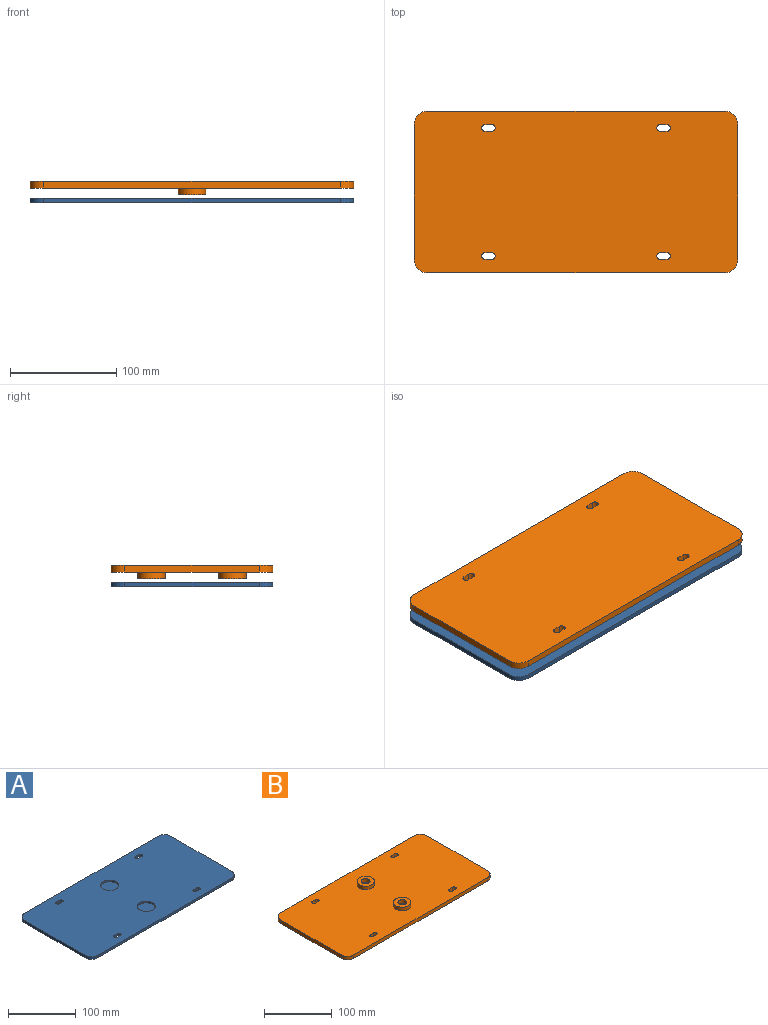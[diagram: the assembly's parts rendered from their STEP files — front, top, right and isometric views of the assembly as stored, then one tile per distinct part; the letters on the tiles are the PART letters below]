
ASSEMBLY  parts=2 mates=1
PART A: 30 faces, bbox 304.8x152.4x4.4 mm
  f0: plane 304.8x152.4mm, normal (0,0,1), area 44907.8mm2, adj f1,f2,f3,f4,f5,f6,f7,f8
  f1: plane 127x4.35mm, normal (1,0,0), area 552.5mm2, adj f0,f25,f28,f29
  f2: plane 279.4x4.35mm, normal (0,1,0), area 1215.4mm2, adj f0,f25,f26,f29
  f3: plane 127x4.35mm, normal (-1,0,0), area 552.5mm2, adj f0,f26,f27,f29
  f4: plane 279.4x4.35mm, normal (0,-1,0), area 1215.4mm2, adj f0,f27,f28,f29
  f5: plane 6.35x4.35mm, normal (0,-1,0), area 27.6mm2, adj f0,f6,f8,f29
  f6: cylinder r=3.17mm len=6.35mm, axis (0,0,1), area 43.4mm2, adj f0,f5,f7,f29
  f7: plane 6.35x4.35mm, normal (0,1,0), area 27.6mm2, adj f0,f6,f8,f29
  f8: cylinder r=3.17mm len=6.35mm, axis (0,0,1), area 43.4mm2, adj f0,f5,f7,f29
  f9: cylinder r=3.17mm len=6.35mm, axis (0,0,1), area 43.4mm2, adj f0,f10,f12,f29
  f10: plane 6.35x4.35mm, normal (0,-1,0), area 27.6mm2, adj f0,f9,f11,f29
  f11: cylinder r=3.17mm len=6.35mm, axis (0,0,1), area 43.4mm2, adj f0,f10,f12,f29
  f12: plane 6.35x4.35mm, normal (0,1,0), area 27.6mm2, adj f0,f9,f11,f29
  f13: cylinder r=3.17mm len=6.35mm, axis (0,0,1), area 43.4mm2, adj f0,f14,f16,f29
  f14: plane 6.35x4.35mm, normal (0,-1,0), area 27.6mm2, adj f0,f13,f15,f29
  f15: cylinder r=3.17mm len=6.35mm, axis (0,0,1), area 43.4mm2, adj f0,f14,f16,f29
  f16: plane 6.35x4.35mm, normal (0,1,0), area 27.6mm2, adj f0,f13,f15,f29
  f17: cylinder r=3.17mm len=6.35mm, axis (0,0,1), area 43.4mm2, adj f0,f18,f20,f29
  f18: plane 6.35x4.35mm, normal (0,-1,0), area 27.6mm2, adj f0,f17,f19,f29
  f19: cylinder r=3.17mm len=6.35mm, axis (0,0,1), area 43.4mm2, adj f0,f18,f20,f29
  f20: plane 6.35x4.35mm, normal (0,1,0), area 27.6mm2, adj f0,f17,f19,f29
  f21: cylinder r=13.33mm len=26.67mm, axis (0,0,1), area 266mm2, adj f0,f22
  f22: plane 26.67x26.67mm, normal (0,0,1), area 558.6mm2, adj f21
  f23: cylinder r=13.33mm len=26.67mm, axis (0,0,1), area 266mm2, adj f0,f24
  f24: plane 26.67x26.67mm, normal (0,0,1), area 558.6mm2, adj f23
  f25: cylinder r=12.7mm len=12.7mm, axis (0,0,1), area 86.8mm2, adj f0,f1,f2,f29
  f26: cylinder r=12.7mm len=12.7mm, axis (0,0,-1), area 86.8mm2, adj f0,f2,f3,f29
  f27: cylinder r=12.7mm len=12.7mm, axis (0,0,1), area 86.8mm2, adj f0,f3,f4,f29
  f28: cylinder r=12.7mm len=12.7mm, axis (0,0,-1), area 86.8mm2, adj f0,f1,f4,f29
  f29: plane 304.8x152.4mm, normal (0,0,-1), area 46025.1mm2, adj f1,f2,f3,f4,f5,f6,f7,f8
PART B: 34 faces, bbox 304.8x152.4x12.7 mm
  f0: plane 304.8x152.4mm, normal (0,0,1), area 44991.3mm2, adj f2,f3,f4,f5,f6,f7,f8,f9
  f1: plane 304.8x152.4mm, normal (0,0,-1), area 46025.1mm2, adj f2,f3,f4,f5,f6,f7,f8,f9
  f2: plane 279.4x6.35mm, normal (0,-1,0), area 1774.2mm2, adj f0,f1,f30,f33
  f3: plane 127x6.35mm, normal (1,0,0), area 806.5mm2, adj f0,f1,f30,f31
  f4: plane 279.4x6.35mm, normal (0,1,0), area 1774.2mm2, adj f0,f1,f31,f32
  f5: plane 127x6.35mm, normal (-1,0,0), area 806.5mm2, adj f0,f1,f32,f33
  f6: plane 6.35x6.35mm, normal (0,-1,0), area 40.3mm2, adj f0,f1,f7,f9
  f7: cylinder r=3.17mm len=6.35mm, axis (0,0,1), area 63.3mm2, adj f0,f1,f6,f8
  f8: plane 6.35x6.35mm, normal (0,1,0), area 40.3mm2, adj f0,f1,f7,f9
  f9: cylinder r=3.17mm len=6.35mm, axis (0,0,1), area 63.3mm2, adj f0,f1,f6,f8
  f10: cylinder r=3.17mm len=6.35mm, axis (0,0,1), area 63.3mm2, adj f0,f1,f11,f13
  f11: plane 6.35x6.35mm, normal (0,-1,0), area 40.3mm2, adj f0,f1,f10,f12
  f12: cylinder r=3.17mm len=6.35mm, axis (0,0,1), area 63.3mm2, adj f0,f1,f11,f13
  f13: plane 6.35x6.35mm, normal (0,1,0), area 40.3mm2, adj f0,f1,f10,f12
  f14: cylinder r=3.17mm len=6.35mm, axis (0,0,1), area 63.3mm2, adj f0,f1,f15,f17
  f15: plane 6.35x6.35mm, normal (0,-1,0), area 40.3mm2, adj f0,f1,f14,f16
  f16: cylinder r=3.17mm len=6.35mm, axis (0,0,1), area 63.3mm2, adj f0,f1,f15,f17
  f17: plane 6.35x6.35mm, normal (0,1,0), area 40.3mm2, adj f0,f1,f14,f16
  f18: cylinder r=3.17mm len=6.35mm, axis (0,0,1), area 63.3mm2, adj f0,f1,f19,f21
  f19: plane 6.35x6.35mm, normal (0,-1,0), area 40.3mm2, adj f0,f1,f18,f20
  f20: cylinder r=3.17mm len=6.35mm, axis (0,0,1), area 63.3mm2, adj f0,f1,f19,f21
  f21: plane 6.35x6.35mm, normal (0,1,0), area 40.3mm2, adj f0,f1,f18,f20
  f22: cylinder r=6.35mm len=12.7mm, axis (0,0,-1), area 253.4mm2, adj f24,f25
  f23: cylinder r=12.83mm len=25.65mm, axis (0,0,-1), area 511.8mm2, adj f0,f24
  f24: plane 25.65x25.65mm, normal (0,0,1), area 390.2mm2, adj f22,f23
  f25: plane 12.7x12.7mm, normal (0,0,1), area 126.7mm2, adj f22
  f26: cylinder r=6.35mm len=12.7mm, axis (0,0,-1), area 253.4mm2, adj f28,f29
  f27: cylinder r=12.83mm len=25.65mm, axis (0,0,-1), area 511.8mm2, adj f0,f28
  f28: plane 25.65x25.65mm, normal (0,0,1), area 390.2mm2, adj f26,f27
  f29: plane 12.7x12.7mm, normal (0,0,1), area 126.7mm2, adj f26
  f30: cylinder r=12.7mm len=12.7mm, axis (0,0,-1), area 126.7mm2, adj f0,f1,f2,f3
  f31: cylinder r=12.7mm len=12.7mm, axis (0,0,1), area 126.7mm2, adj f0,f1,f3,f4
  f32: cylinder r=12.7mm len=12.7mm, axis (0,0,-1), area 126.7mm2, adj f0,f1,f4,f5
  f33: cylinder r=12.7mm len=12.7mm, axis (0,0,1), area 126.7mm2, adj f0,f1,f2,f5
PLACE A t=(95.43,-86.09,-92.51)mm
PLACE B rot(axis=(1,0,0),180deg) t=(95.43,-51.72,-70.29)mm
MATE fastened B.f22 <-> A.f21  axis (0,0,-1) through (96.9,-107.01,-82.99)mm
